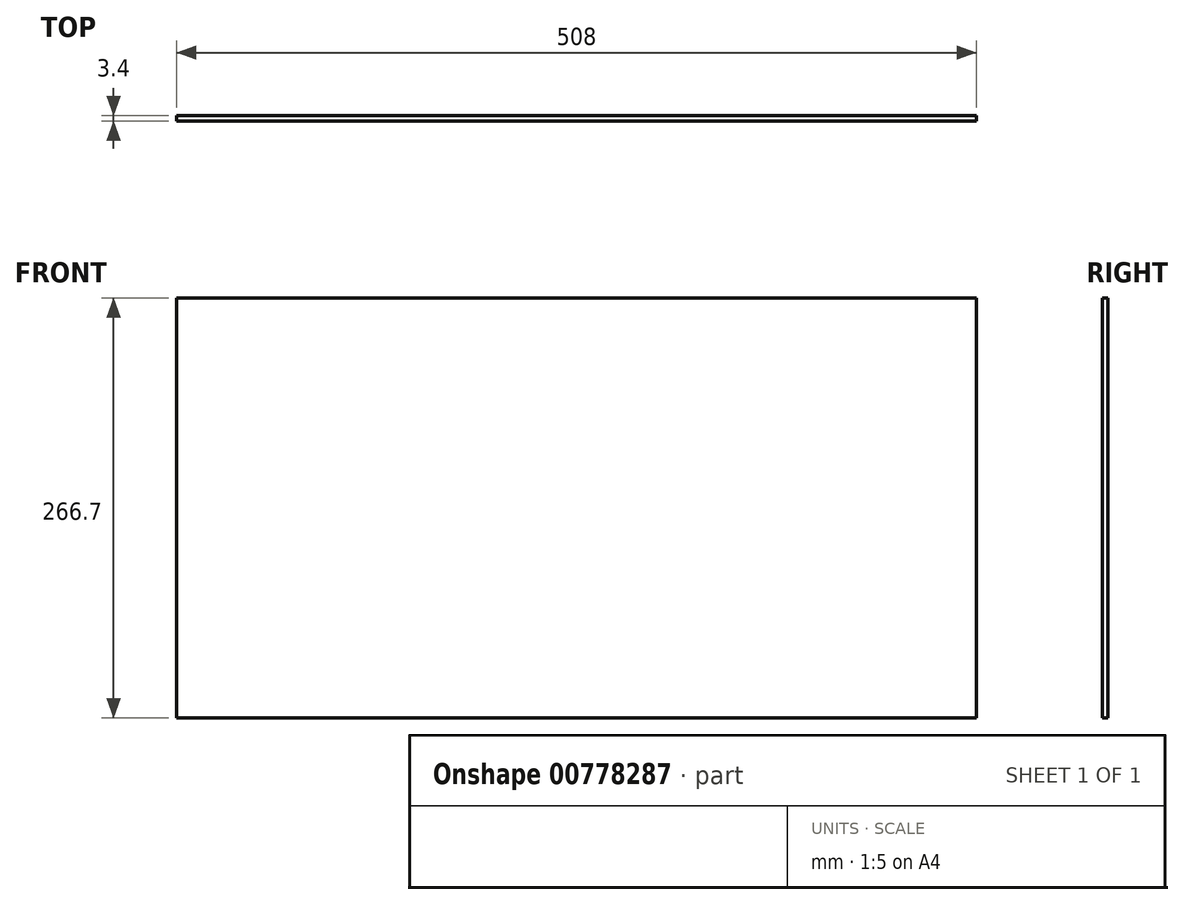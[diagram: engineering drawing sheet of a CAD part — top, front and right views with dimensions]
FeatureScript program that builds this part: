
annotation { "Feature Type Name" : "Feature", "Feature Type Description" : "" }
export const myFeature = defineFeature(function(context is Context, id is Id, definition is map)
    precondition{}
    {
        {
            var Q0;
            Q0=qCreatedBy(makeId("Front.planeOp"),FACE);
            var sketch = newSketch(context, id + "F0", { "sketchPlane" : qUnion([Q0])});
            skLineSegment(sketch, "E0.bottom", {"start": v(-254, 133.35) * mm, "end": v(254, 133.35) * mm});
            skLineSegment(sketch, "E0.top", {"start": v(-254, -133.35) * mm, "end": v(254, -133.35) * mm});
            skLineSegment(sketch, "E0.left", {"start": v(-254, 133.35) * mm, "end": v(-254, -133.35) * mm});
            skLineSegment(sketch, "E0.right", {"start": v(254, 133.35) * mm, "end": v(254, -133.35) * mm});
            skPoint(sketch, "E0.middle", {"position": v(0, 0) * mm});
            skSolve(sketch);
        }
        {
            var Q0;
            Q0=makeQuery(id+"F0.imprint","IMPRINT",FACE,{"disambiguationData":[TD([[makeQuery(id+"F0.imprint","IMPRINT",EDGE,{"derivedFrom":sQuery(id+"F0.wireOp",EDGE,"E0.bottom")}),-1.0]])]});
            extrude(context, id + "F1", {"entities" : qUnion([Q0]), "depth" : 3.4 * mm, "offsetDistance" : 25.4 * mm});
        }
    });
